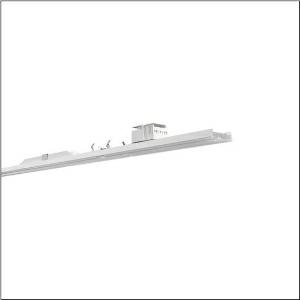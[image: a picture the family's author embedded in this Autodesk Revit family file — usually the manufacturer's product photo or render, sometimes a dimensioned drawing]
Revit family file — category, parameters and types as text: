
# Revit family: licross_r__11_recessed_mo_51tl18vn58xf_a930
name_source: partatom
category: Lighting Fixtures
units: mm (PartAtom-declared; Revit-internal decimal feet)

## family parameters
Cut with Voids When Loaded = No
Host = Face
Light Source = No
Part Type = Normal
Room Calculation Point = No
Round Connector Dimension = Use Diameter
Shared = No

## types (1)
- --- (1 x LED, 8030 lm, 49.4 W, 5000K)
    Apparent Load = 49 VA
    CIE Flux Codes = 83 96 99 100 100
    Color Rendering = 80
    Color Temperature = 5000K
    Default Elevation = 1800 mm
    Description = Licross® 11 Recessed MOluminaire insert, length: 1.500mm, width: 66mm, height: 67mm, LED rated luminous flux: 8.030lm, light colour: 850, control gear: DALI 2, CLO, control gear: ECG DALI, with plug, 5-pole, with phase selection, mains connection: 220..240V, AC, 50/60Hz, halogen-free wiring, primary optical cover: cover, of PMMA, light emission: direct distribution, protection rating (complete): IP40, insulation class (complete): insulation class I (protective earthing), certification: CE, ENEC, VDE, UKCA, protection symbol: D if used in an environment without relevant dust loads with corresponding accessories, permissible ambient temperature for indoor applications: -25..+35°C, corresponds to IFS (International Featured Standards) requirements for safety and quality in the food industry, reducing of maximum allowable ambient temperature of 5°C with ceiling mounting, packaging unit: 1 piece
    Height = 58 mm
    Lamp = 1 x LED
    Lamp Light Flux = 8030 lm
    Lamp Power = 49.4 W
    Lamp count = 1
    Length = 1500 mm
    Luminous efficacy = 163 lm/W
    Manufacturer = Siteco
    ModVariant = No
    Model = 51TL18VN58XF
    Mounting Place = Ceiling
    Mounting Type = Pendant
    Number of Poles = 1
    OnlyDefault = Yes
    Power Factor = 1
    Product Name = Licross® 11 Recessed MO
    Product group = luminaire insert
    ProductGroupID = 902
    Protection Class = Protection class I
    Protection Degree = IP 40
    RLX_Detail_Level = 1
    RlxData = <blob elided: 22377 chars, md5=1e57ab82>
    Socket = socket
    Standby Power = 0 W
    System Light Flux = 8030 lm
    System Power = 49 W
    Type Comments = factory setting: luminous flux: 100 % | dim-lin: 254 | 325 mA
    Type Image = l_1266722.jpg
    URL = http://relux.com
    VarID = @adj_128987
    Voltage = 0 V
    Weight = 0.00 kg
    Width = 66 mm

## geometry (parser evidence)
native form markers: Blend x4, Sweep x11
no freeform markers — native parametric forms only
